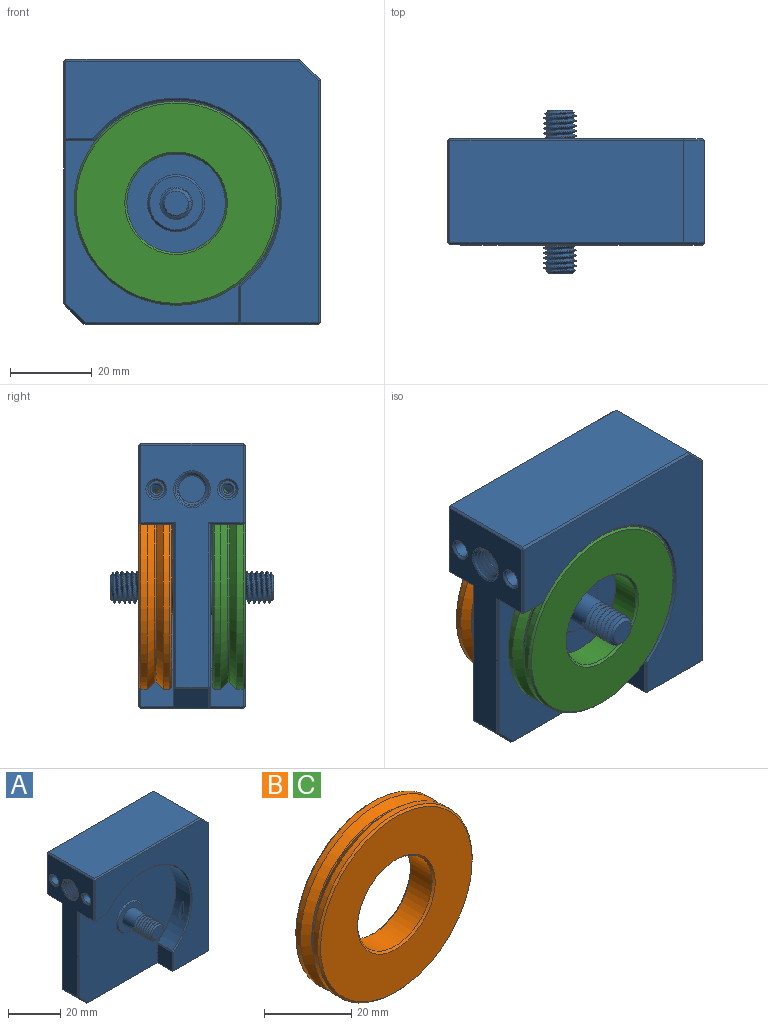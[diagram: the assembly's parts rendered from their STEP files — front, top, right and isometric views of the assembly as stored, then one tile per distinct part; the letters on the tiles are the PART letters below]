
ASSEMBLY  parts=3 mates=1
PART A: 127 faces, bbox 63.2x41.4x65.5 mm
  f0: cylinder r=3.3mm len=14mm, axis (-1,0,0), area 69.4mm2, adj f61,f65,f67,f68,f69
  f1: cylinder r=3.3mm len=14mm, axis (0,0,-1), area 69.4mm2, adj f60,f62,f63,f64,f66
  f2: cylinder r=3.95mm len=7.9mm, axis (0,1,0), area 139.6mm2, adj f3,f48,f57,f58
  f3: cylinder r=3.95mm len=7.9mm, axis (0,1,0), area 3.7mm2, adj f2,f4,f58,f59
  f4: cylinder r=3.95mm len=7.9mm, axis (0,1,0), area 3.7mm2, adj f3,f5,f58,f59
  f5: cylinder r=3.95mm len=7.9mm, axis (0,1,0), area 3.7mm2, adj f4,f6,f58,f59
  f6: cylinder r=3.95mm len=7.9mm, axis (0,1,0), area 3.7mm2, adj f5,f7,f58,f59
  f7: cylinder r=3.95mm len=7.9mm, axis (0,1,0), area 3.7mm2, adj f6,f8,f58,f59
  f8: cylinder r=3.95mm len=7.9mm, axis (0,1,0), area 3.7mm2, adj f7,f9,f58,f59
  f9: cylinder r=3.95mm len=5.61mm, axis (0,1,0), area 1mm2, adj f8,f55,f58,f59
  f10: cylinder r=1.08mm len=16.33mm, axis (0,0,-1), area 80.9mm2, adj f20,f75
  f11: cylinder r=1mm len=15.71mm, axis (0,0,-1), area 74.2mm2, adj f18,f76
  f12: plane 57.01x25mm, normal (0,0,-1), area 675.2mm2, adj f79,f80,f84,f92,f98,f99,f105,f106
  f13: plane 59.29x25mm, normal (-1,0,0), area 693.5mm2, adj f94,f101,f107,f111,f112,f115,f118,f119
  f14: plane 54.5x52.22mm, normal (0,-1,0), area 2263.1mm2, adj f16,f17,f18,f90,f104,f105,f114,f119
  f15: plane 54.5x52.22mm, normal (0,1,0), area 2266.1mm2, adj f19,f20,f21,f70,f72,f99,f111
  f16: plane 8.88x8mm, normal (-1,0,0), area 71mm2, adj f14,f89,f90,f98
  f17: plane 8x6.6mm, normal (0,0,-1), area 52.8mm2, adj f14,f104,f113,f118
  f18: cylinder r=25.25mm len=45.23mm, axis (0,1,0), area 664mm2, adj f11,f14,f36,f90,f103,f104
  f19: plane 8x6.85mm, normal (0,0,-1), area 54.8mm2, adj f15,f20,f93,f107
  f20: cylinder r=25.25mm len=45.37mm, axis (0,1,0), area 666.4mm2, adj f10,f15,f19,f21,f37,f86
  f21: plane 9.13x8mm, normal (-1,0,0), area 73mm2, adj f15,f20,f81,f92
  f22: plane 59.5x25mm, normal (1,0,0), area 1487.5mm2, adj f71,f78,f79,f88
  f23: plane 57.22x25mm, normal (0,0,1), area 1430.5mm2, adj f71,f87,f101,f102
  f24: plane 64x61.72mm, normal (0,-1,0), area 1459.6mm2, adj f84,f88,f89,f96,f102,f103,f112,f113
  f25: plane 64x61.72mm, normal (0,1,0), area 1459.6mm2, adj f78,f80,f81,f82,f86,f87,f93,f94
  f26: plane 4.05x4.05mm, normal (0,0,-1), area 5.8mm2, adj f27,f76
  f27: cylinder r=2.02mm len=9.5mm, axis (0,0,-1), area 120.9mm2, adj f26,f126
  f28: plane 4.05x4.05mm, normal (0,0,-1), area 5mm2, adj f29,f75
  f29: cylinder r=2.02mm len=9.5mm, axis (0,0,-1), area 120.9mm2, adj f28,f125
  f30: cylinder r=2.02mm len=9.5mm, axis (-1,0,0), area 120.9mm2, adj f31,f121
  f31: plane 4.05x4.05mm, normal (-1,0,0), area 5.8mm2, adj f30,f74
  f32: cylinder r=2.02mm len=9.5mm, axis (-1,0,0), area 120.9mm2, adj f33,f122
  f33: plane 4.05x4.05mm, normal (-1,0,0), area 5.8mm2, adj f32,f73
  f34: cylinder r=1mm len=13.41mm, axis (-1,0,0), area 56mm2, adj f37,f73
  f35: cylinder r=1mm len=13.41mm, axis (-1,0,0), area 56mm2, adj f36,f74
  f36: bspline ~7.78x2.4mm, area 4.7mm2, adj f18,f35
  f37: bspline ~7.78x2.4mm, area 4.7mm2, adj f20,f34
  f38: plane 13x13mm, normal (0,1,0), area 83.7mm2, adj f47,f72
  f39: plane 5.9x5.9mm, normal (0,1,0), area 27.3mm2, adj f50
  f40: cylinder r=3.95mm len=5.84mm, axis (0,1,0), area 1.1mm2, adj f41,f50,f51,f53,f54
  f41: cylinder r=3.95mm len=7.9mm, axis (0,1,0), area 4.3mm2, adj f40,f42,f53,f54
  f42: cylinder r=3.95mm len=7.9mm, axis (0,1,0), area 4.3mm2, adj f41,f43,f53,f54
  f43: cylinder r=3.95mm len=7.9mm, axis (0,1,0), area 4.3mm2, adj f42,f44,f53,f54
  f44: cylinder r=3.95mm len=7.9mm, axis (0,1,0), area 4.3mm2, adj f43,f45,f53,f54
  f45: cylinder r=3.95mm len=7.9mm, axis (0,1,0), area 4.3mm2, adj f44,f46,f53,f54
  f46: cylinder r=3.95mm len=7.9mm, axis (0,1,0), area 4.3mm2, adj f45,f47,f53,f54
  f47: cylinder r=3.95mm len=7.9mm, axis (0,1,0), area 139.9mm2, adj f38,f46,f52,f53
  f48: plane 13x13mm, normal (0,-1,0), area 83.7mm2, adj f2,f123
  f49: plane 5.9x5.9mm, normal (0,-1,0), area 27.3mm2, adj f56
  f50: cone r=3.95mm half-angle=45deg, axis (0,-1,0), area 17.5mm2, adj f39,f40,f51,f53,f54
  f51: cone r=3.95mm half-angle=45deg, axis (0,-1,0), area 0.2mm2, adj f40,f50,f53
  f52: plane 1.08x0.93mm, normal (0,0,-1), area 0.5mm2, adj f47,f53,f54
  f53: bspline ~10.13x9.17mm, area 173.1mm2, adj f40,f41,f42,f43,f44,f45,f46,f47
  f54: bspline ~10.13x9.17mm, area 163.5mm2, adj f40,f41,f42,f43,f44,f45,f46,f50
  f55: cone r=2.95mm half-angle=45deg, axis (0,1,0), area 4.4mm2, adj f9,f56,f58,f59
  f56: cone r=2.95mm half-angle=45deg, axis (0,1,0), area 12.7mm2, adj f49,f55,f59
  f57: plane 1.1x0.95mm, normal (0,0,-1), area 0.5mm2, adj f2,f58,f59
  f58: bspline ~10.13x9.12mm, area 176.8mm2, adj f2,f3,f4,f5,f6,f7,f8,f9
  f59: bspline ~10.13x9.12mm, area 166.6mm2, adj f3,f4,f5,f6,f7,f8,f9,f55
  f60: plane 6.6x6.6mm, normal (0,0,-1), area 34.2mm2, adj f1
  f61: plane 6.6x6.6mm, normal (-1,0,0), area 34.2mm2, adj f0
  f62: plane 1.1x0.95mm, normal (0,-1,0), area 0.5mm2, adj f1,f63,f64
  f63: bspline ~14.93x9.82mm, area 297mm2, adj f1,f62,f64,f66,f124
  f64: bspline ~14.93x9.82mm, area 287.1mm2, adj f1,f62,f63,f66,f124
  f65: cone r=3.3mm half-angle=45deg, axis (-1,0,0), area 15mm2, adj f0,f68,f69,f120
  f66: cone r=3.3mm half-angle=45deg, axis (0,0,-1), area 15mm2, adj f1,f63,f64,f124
  f67: plane 1.1x0.95mm, normal (0,-1,0), area 0.5mm2, adj f0,f68,f69
  f68: bspline ~14.93x9.82mm, area 297mm2, adj f0,f65,f67,f69,f120
  f69: bspline ~14.93x9.82mm, area 287.1mm2, adj f0,f65,f67,f68,f120
  f70: plane 8.5x4.71mm, normal (-0.71,0,-0.71), area 56.4mm2, adj f15,f99,f106,f111,f114,f115
  f71: plane 25x5mm, normal (0.71,0,0.71), area 176.8mm2, adj f22,f23,f82,f96
  f72: cone r=7mm half-angle=45deg, axis (0,-1,0), area 30mm2, adj f15,f38
  f73: cone r=1mm half-angle=45deg, axis (-1,0,0), area 5.6mm2, adj f33,f34
  f74: cone r=1mm half-angle=45deg, axis (-1,0,0), area 5.6mm2, adj f31,f35
  f75: cone r=1.58mm half-angle=45deg, axis (0,0,-1), area 5.9mm2, adj f10,f28
  f76: cone r=1.5mm half-angle=45deg, axis (0,0,-1), area 5.6mm2, adj f11,f26
  f77: plane 0.5x0.5mm, normal (0.58,0.58,-0.58), area 0.2mm2, adj f78,f79,f80
  f78: plane 59.5x0.5mm, normal (0.71,0.71,0), area 42mm2, adj f22,f25,f77,f82
  f79: plane 25x0.5mm, normal (0.71,0,-0.71), area 17.7mm2, adj f12,f22,f77,f83
  f80: plane 19x0.5mm, normal (0,0.71,-0.71), area 13.4mm2, adj f12,f25,f77,f85
  f81: plane 9.13x0.5mm, normal (-0.71,0.71,0), area 6.4mm2, adj f21,f25,f85,f86
  f82: plane 5.21x5.21mm, normal (0.5,0.71,0.5), area 4.9mm2, adj f25,f71,f78,f87
  f83: plane 0.5x0.5mm, normal (0.58,-0.58,-0.58), area 0.2mm2, adj f79,f84,f88
  f84: plane 19x0.5mm, normal (0,-0.71,-0.71), area 13.4mm2, adj f12,f24,f83,f91
  f85: plane 0.5x0.5mm, normal (-0.58,0.58,-0.58), area 0.2mm2, adj f80,f81,f92
  f86: cone r=25.75mm half-angle=45deg, axis (0,1,0), area 61.4mm2, adj f20,f25,f81,f93
  f87: plane 57.22x0.5mm, normal (0,0.71,0.71), area 40.4mm2, adj f23,f25,f82,f95
  f88: plane 59.5x0.5mm, normal (0.71,-0.71,0), area 42mm2, adj f22,f24,f83,f96
  f89: plane 8.88x0.5mm, normal (-0.71,-0.71,0), area 6.3mm2, adj f16,f24,f91,f97
  f90: plane 8x0.4mm, normal (-0.9,0,0.44), area 3.5mm2, adj f14,f16,f18,f97
  f91: plane 0.5x0.5mm, normal (-0.58,-0.58,-0.58), area 0.2mm2, adj f84,f89,f98
  f92: plane 8.5x0.5mm, normal (-0.71,0,-0.71), area 5.8mm2, adj f12,f21,f85,f99
  f93: plane 6.85x0.5mm, normal (0,0.71,-0.71), area 4.8mm2, adj f19,f25,f86,f100
  f94: plane 19x0.5mm, normal (-0.71,0.71,0), area 13.4mm2, adj f13,f25,f95,f100
  f95: plane 0.5x0.5mm, normal (-0.58,0.58,0.58), area 0.2mm2, adj f87,f94,f101
  f96: plane 5.21x5.21mm, normal (0.5,-0.71,0.5), area 4.9mm2, adj f24,f71,f88,f102
  f97: plane 0.5x0.5mm, normal (-0.67,-0.67,0.33), area 0.1mm2, adj f89,f90,f103
  f98: plane 8.5x0.5mm, normal (-0.71,0,-0.71), area 5.8mm2, adj f12,f16,f91,f105
  f99: plane 38.72x0.5mm, normal (0,0.71,-0.71), area 27mm2, adj f12,f15,f70,f92,f106
  f100: plane 0.5x0.5mm, normal (-0.58,0.58,-0.58), area 0.2mm2, adj f93,f94,f107
  f101: plane 25x0.5mm, normal (-0.71,0,0.71), area 17.7mm2, adj f13,f23,f95,f108
  f102: plane 57.22x0.5mm, normal (0,-0.71,0.71), area 40.4mm2, adj f23,f24,f96,f108
  f103: cone r=25.25mm half-angle=45deg, axis (0,-1,0), area 61.2mm2, adj f18,f24,f97,f109
  f104: plane 8x0.4mm, normal (0.44,0,-0.9), area 3.5mm2, adj f14,f17,f18,f109
  f105: plane 38.01x0.5mm, normal (0,-0.71,-0.71), area 26.7mm2, adj f12,f14,f98,f110
  f106: plane 8.15x0.35mm, normal (-0.38,0,-0.92), area 3.1mm2, adj f12,f70,f99,f110
  f107: plane 8.5x0.5mm, normal (-0.71,0,-0.71), area 5.8mm2, adj f13,f19,f100,f111
  f108: plane 0.5x0.5mm, normal (-0.58,-0.58,0.58), area 0.2mm2, adj f101,f102,f112
  f109: plane 0.5x0.5mm, normal (0.33,-0.67,-0.67), area 0.1mm2, adj f103,f104,f113
  f110: plane 0.5x0.5mm, normal (-0.28,-0.68,-0.68), area 0.1mm2, adj f105,f106,f114
  f111: plane 41x0.5mm, normal (-0.71,0.71,0), area 28.6mm2, adj f13,f15,f70,f107,f115
  f112: plane 19x0.5mm, normal (-0.71,-0.71,0), area 13.4mm2, adj f13,f24,f108,f116
  f113: plane 6.6x0.5mm, normal (0,-0.71,-0.71), area 4.7mm2, adj f17,f24,f109,f116
  f114: plane 5.06x5.06mm, normal (-0.5,-0.71,-0.5), area 4.7mm2, adj f14,f70,f110,f117
  f115: plane 8.15x0.35mm, normal (-0.92,0,-0.38), area 3.1mm2, adj f13,f70,f111,f117
  f116: plane 0.5x0.5mm, normal (-0.58,-0.58,-0.58), area 0.2mm2, adj f112,f113,f118
  f117: plane 0.5x0.5mm, normal (-0.68,-0.68,-0.28), area 0.1mm2, adj f114,f115,f119
  f118: plane 8.5x0.5mm, normal (-0.71,0,-0.71), area 5.8mm2, adj f13,f17,f116,f119
  f119: plane 40.29x0.5mm, normal (-0.71,-0.71,0), area 28.3mm2, adj f13,f14,f117,f118
  f120: cone r=4.51mm half-angle=67.5deg, axis (-1,0,0), area 10.3mm2, adj f13,f65,f68,f69
  f121: cone r=2.02mm half-angle=45deg, axis (-1,0,0), area 10.1mm2, adj f13,f30
  f122: cone r=2.02mm half-angle=45deg, axis (-1,0,0), area 10.1mm2, adj f13,f32
  f123: cone r=6.5mm half-angle=45deg, axis (0,1,0), area 30mm2, adj f14,f48
  f124: cone r=4.51mm half-angle=67.5deg, axis (0,0,-1), area 10.3mm2, adj f12,f63,f64,f66
  f125: cone r=2.02mm half-angle=45deg, axis (0,0,-1), area 10.1mm2, adj f12,f29
  f126: cone r=2.02mm half-angle=45deg, axis (0,0,-1), area 10.1mm2, adj f12,f27
PART B: 12 faces, bbox 50x8x50 mm
  f0: cylinder r=25mm len=50mm, axis (0,1,0), area 235.6mm2, adj f7,f9
  f1: cylinder r=25mm len=50mm, axis (0,1,0), area 235.6mm2, adj f6,f11
  f2: cylinder r=12.05mm len=24.1mm, axis (0,1,0), area 530mm2, adj f8,f10
  f3: plane 49x49mm, normal (0,-1,0), area 1390.9mm2, adj f10,f11
  f4: plane 49x49mm, normal (0,1,0), area 1390.9mm2, adj f8,f9
  f5: cylinder r=23.2mm len=46.4mm, axis (0,-1,0), area 58.3mm2, adj f6,f7
  f6: cone r=25mm half-angle=45deg, axis (0,-1,0), area 385.5mm2, adj f1,f5
  f7: cone r=24.5mm half-angle=45deg, axis (0,1,0), area 385.5mm2, adj f0,f5
  f8: cone r=12.55mm half-angle=45deg, axis (0,1,0), area 54.6mm2, adj f2,f4
  f9: cone r=25mm half-angle=45deg, axis (0,-1,0), area 110mm2, adj f0,f4
  f10: cone r=12.05mm half-angle=45deg, axis (0,-1,0), area 54.6mm2, adj f2,f3
  f11: cone r=24.5mm half-angle=45deg, axis (0,1,0), area 110mm2, adj f1,f3
PART C: same geometry as B
PLACE A t=(4.82,-4.28,2.23)mm
PLACE B t=(4.82,4.72,2.23)mm
PLACE C t=(4.82,-13.28,2.23)mm
MATE planar C.f0 <-> A.f72  axis (0,1,0) through (4.82,-9.28,2.23)mm
